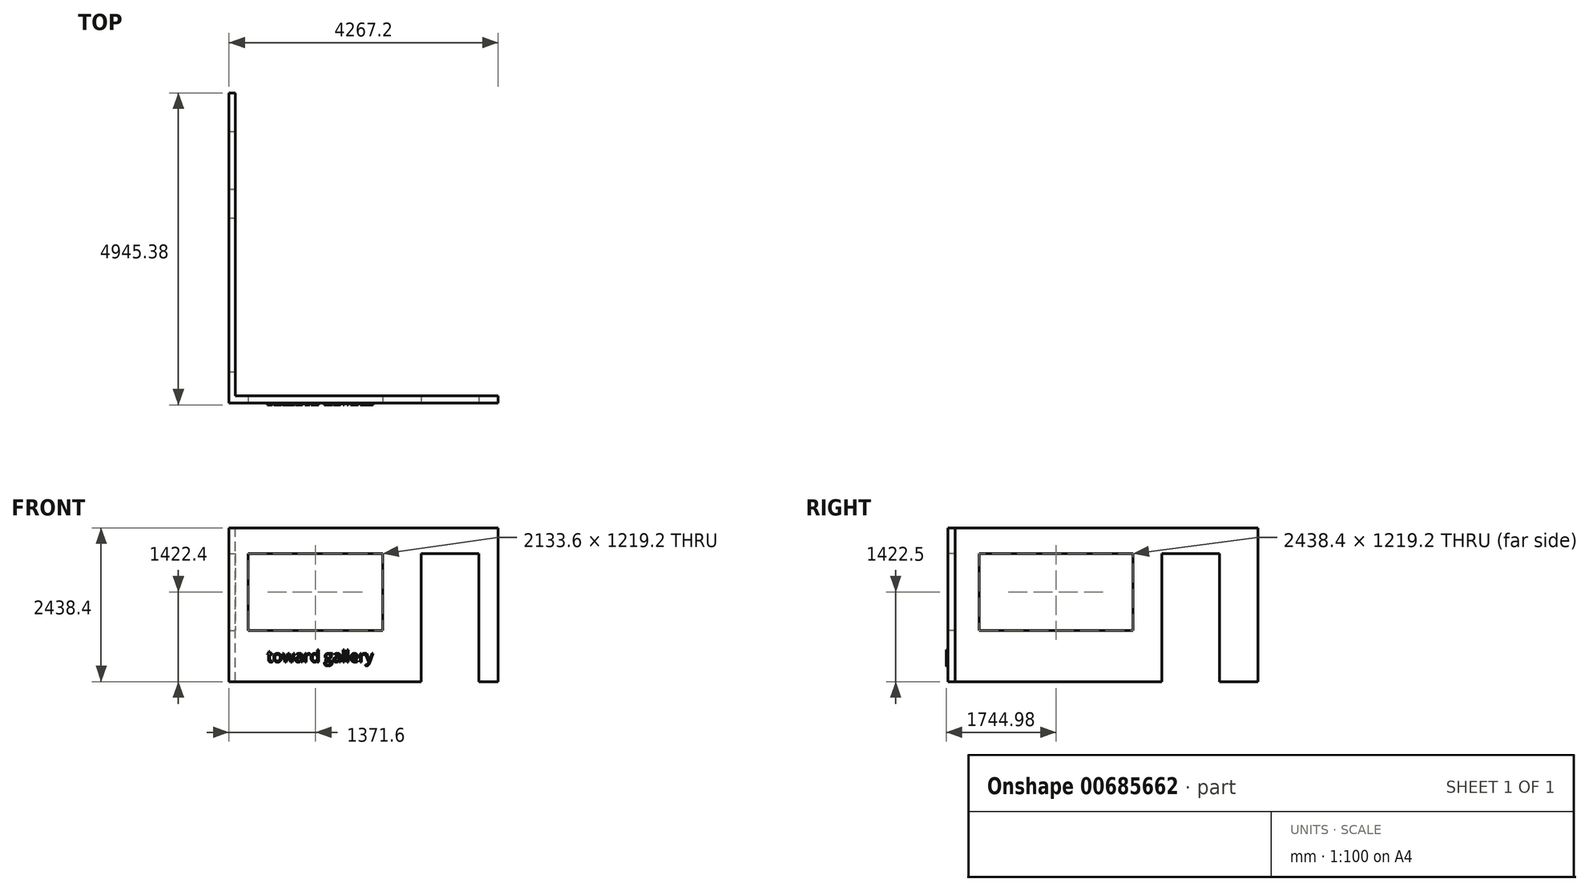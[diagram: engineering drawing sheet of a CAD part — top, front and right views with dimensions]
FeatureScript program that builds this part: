
annotation { "Feature Type Name" : "Feature", "Feature Type Description" : "" }
export const myFeature = defineFeature(function(context is Context, id is Id, definition is map)
    precondition{}
    {
        {
            var Q0;
            Q0=qCreatedBy(makeId("Front.planeOp"),FACE);
            var sketch = newSketch(context, id + "F0", { "sketchPlane" : qUnion([Q0])});
            skLineSegment(sketch, "E0.bottom", {"start": v(0, 0) * mm, "end": v(4267.2, 0) * mm});
            skLineSegment(sketch, "E0.top", {"start": v(0, 2438.4) * mm, "end": v(4267.2, 2438.4) * mm});
            skLineSegment(sketch, "E0.left", {"start": v(0, 0) * mm, "end": v(0, 2438.4) * mm});
            skLineSegment(sketch, "E0.right", {"start": v(4267.2, 0) * mm, "end": v(4267.2, 2438.4) * mm});
            skSolve(sketch);
        }
        {
            var Q0;
            Q0=makeQuery(id+"F0.imprint","IMPRINT",FACE,{"disambiguationData":[TD([[makeQuery(id+"F0.imprint","IMPRINT",EDGE,{"derivedFrom":sQuery(id+"F0.wireOp",EDGE,"E0.bottom")}),1.0]])]});
            extrude(context, id + "F1", {"entities" : qUnion([Q0]), "depth" : 114.3 * mm, "offsetDistance" : 30.48 * mm});
        }
        {
            var Q0;
            Q0=makeQuery(id+"F1.opExtrude","CAP_FACE",FACE,{"disambiguationData":[OSD([sQuery(id+"F0.wireOp",EDGE,"E0.bottom"),sQuery(id+"F0.wireOp",EDGE,"E0.top"),sQuery(id+"F0.wireOp",EDGE,"E0.left"),sQuery(id+"F0.wireOp",EDGE,"E0.right")])],"isStart":false});
            var sketch = newSketch(context, id + "F2", { "sketchPlane" : qUnion([Q0])});
            skLineSegment(sketch, "E1.bottom", {"start": v(3048, 0) * mm, "end": v(3962.4, 0) * mm});
            skLineSegment(sketch, "E1.top", {"start": v(3048, 2032) * mm, "end": v(3962.4, 2032) * mm});
            skLineSegment(sketch, "E1.left", {"start": v(3048, 0) * mm, "end": v(3048, 2032) * mm});
            skLineSegment(sketch, "E1.right", {"start": v(3962.4, 0) * mm, "end": v(3962.4, 2032) * mm});
            skSolve(sketch);
        }
        {
            var Q0;
            Q0 = qSketchRegion(id + "F2", true);
            extrude(context, id + "F3", {"entities" : qUnion([Q0]), "operationType" : NewBodyOperationType.REMOVE, "endBound" : BoundingType.THROUGH_ALL, "oppositeDirection" : true, "depth" : 30.48 * mm, "offsetDistance" : 30.48 * mm});
        }
        {
            var Q0;
            Q0=makeQuery(id+"F1.opExtrude","CAP_FACE",FACE,{"disambiguationData":[OSD([sQuery(id+"F0.wireOp",EDGE,"E0.bottom"),sQuery(id+"F0.wireOp",EDGE,"E0.top"),sQuery(id+"F0.wireOp",EDGE,"E0.left"),sQuery(id+"F0.wireOp",EDGE,"E0.right")])],"isStart":false});
            var sketch = newSketch(context, id + "F4", { "sketchPlane" : qUnion([Q0])});
            skLineSegment(sketch, "E2.bottom", {"start": v(304.8, 2032) * mm, "end": v(2438.4, 2032) * mm});
            skLineSegment(sketch, "E2.top", {"start": v(304.8, 812.8) * mm, "end": v(2438.4, 812.8) * mm});
            skLineSegment(sketch, "E2.left", {"start": v(304.8, 2032) * mm, "end": v(304.8, 812.8) * mm});
            skLineSegment(sketch, "E2.right", {"start": v(2438.4, 2032) * mm, "end": v(2438.4, 812.8) * mm});
            skSolve(sketch);
        }
        {
            var Q0;
            Q0 = qSketchRegion(id + "F4", true);
            extrude(context, id + "F5", {"entities" : qUnion([Q0]), "operationType" : NewBodyOperationType.REMOVE, "endBound" : BoundingType.THROUGH_ALL, "oppositeDirection" : true, "depth" : 30.48 * mm, "offsetDistance" : 30.48 * mm});
        }
        {
            var Q0;
            Q0=makeQuery(id+"F1.opExtrude","CAP_FACE",FACE,{"disambiguationData":[OSD([sQuery(id+"F0.wireOp",EDGE,"E0.bottom"),sQuery(id+"F0.wireOp",EDGE,"E0.top"),sQuery(id+"F0.wireOp",EDGE,"E0.left"),sQuery(id+"F0.wireOp",EDGE,"E0.right")])],"isStart":true});
            var sketch = newSketch(context, id + "F6", { "sketchPlane" : qUnion([Q0])});
            skLineSegment(sketch, "E3.bottom", {"start": v(0, 0) * mm, "end": v(-101.6, 0) * mm});
            skLineSegment(sketch, "E3.top", {"start": v(0, 2438.4) * mm, "end": v(-101.6, 2438.4) * mm});
            skLineSegment(sketch, "E3.left", {"start": v(0, 0) * mm, "end": v(0, 2438.4) * mm});
            skLineSegment(sketch, "E3.right", {"start": v(-101.6, 0) * mm, "end": v(-101.6, 2438.4) * mm});
            skSolve(sketch);
        }
        {
            var Q0;
            Q0 = qSketchRegion(id + "F6", true);
            extrude(context, id + "F7", {"entities" : qUnion([Q0]), "operationType" : NewBodyOperationType.ADD, "depth" : 4800.6 * mm, "offsetDistance" : 30.48 * mm});
        }
        {
            var Q0;
            Q0=makeQuery(id+"F7.opExtrude","SWEPT_FACE",FACE,{"disambiguationData":[OSD([sQuery(id+"F6.wireOp",EDGE,"E3.right")])]});
            var sketch = newSketch(context, id + "F8", { "sketchPlane" : qUnion([Q0])});
            skLineSegment(sketch, "E4.bottom", {"start": v(4191, 0) * mm, "end": v(3276.6, 0) * mm});
            skLineSegment(sketch, "E4.top", {"start": v(4191, 2032.1) * mm, "end": v(3276.6, 2032.1) * mm});
            skLineSegment(sketch, "E4.left", {"start": v(4191, 0) * mm, "end": v(4191, 2032.1) * mm});
            skLineSegment(sketch, "E4.right", {"start": v(3276.6, 0) * mm, "end": v(3276.6, 2032.1) * mm});
            skLineSegment(sketch, "E5.bottom", {"start": v(2819.4, 2032.1) * mm, "end": v(381, 2032.1) * mm});
            skLineSegment(sketch, "E5.top", {"start": v(2819.4, 812.9) * mm, "end": v(381, 812.9) * mm});
            skLineSegment(sketch, "E5.left", {"start": v(2819.4, 2032.1) * mm, "end": v(2819.4, 812.9) * mm});
            skLineSegment(sketch, "E5.right", {"start": v(381, 2032.1) * mm, "end": v(381, 812.9) * mm});
            skSolve(sketch);
        }
        {
            var Q0;
            Q0 = qSketchRegion(id + "F8", true);
            extrude(context, id + "F9", {"entities" : qUnion([Q0]), "operationType" : NewBodyOperationType.REMOVE, "endBound" : BoundingType.THROUGH_ALL, "oppositeDirection" : true, "depth" : 30.48 * mm, "offsetDistance" : 30.48 * mm});
        }
        {
            var Q0;
            Q0=makeQuery(id+"F1.opExtrude","CAP_FACE",FACE,{"disambiguationData":[OSD([sQuery(id+"F0.wireOp",EDGE,"E0.bottom"),sQuery(id+"F0.wireOp",EDGE,"E0.top"),sQuery(id+"F0.wireOp",EDGE,"E0.left"),sQuery(id+"F0.wireOp",EDGE,"E0.right")])],"isStart":false});
            var sketch = newSketch(context, id + "F10", { "sketchPlane" : qUnion([Q0])});
            skText(sketch, "E6", { "text": "toward gallery\n", "fontName": "OpenSans-Regular.ttf"});
            const initialGuessF10  = {"E6": [0.60435, 0.31269, 1, 0, 0.1822]};
            skSetInitialGuess(sketch, initialGuessF10);
            skSolve(sketch);
        }
        {
            var Q0;
            Q0 = qSketchRegion(id + "F10", true);
            extrude(context, id + "F11", {"entities" : qUnion([Q0]), "operationType" : NewBodyOperationType.ADD, "depth" : 30.48 * mm, "offsetDistance" : 30.48 * mm});
        }
    });
